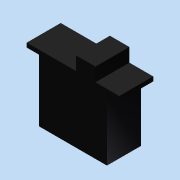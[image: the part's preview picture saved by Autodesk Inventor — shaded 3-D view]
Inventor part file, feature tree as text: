
AUTODESK INVENTOR PART (.ipt)
format: ipt  version: 2012 (Build 160160000, 160)  size: 82,944 bytes
history: native  units: in
note: dims shown in document units (in); Inventor stores cm internally (conversion verified against a paired STEP export)
features: extrude x1, sketch x1
ambient origin geometry x8: Origin, YZ Plane, XZ Plane, XY Plane, X Axis, Y Axis, Z Axis, Center Point
bodies: Solid1 (feature_tree)
feature tree (2):
  extrude  "Extrusion1"  Depth=1.5748in
  sketch  "Sketch1"  dims[d7=1.8543in d8=1.5748in d9=1.5394in d10=2.1457in d11=1.5394in d12=0.1in d13=0.7874in d14=0.0in]
